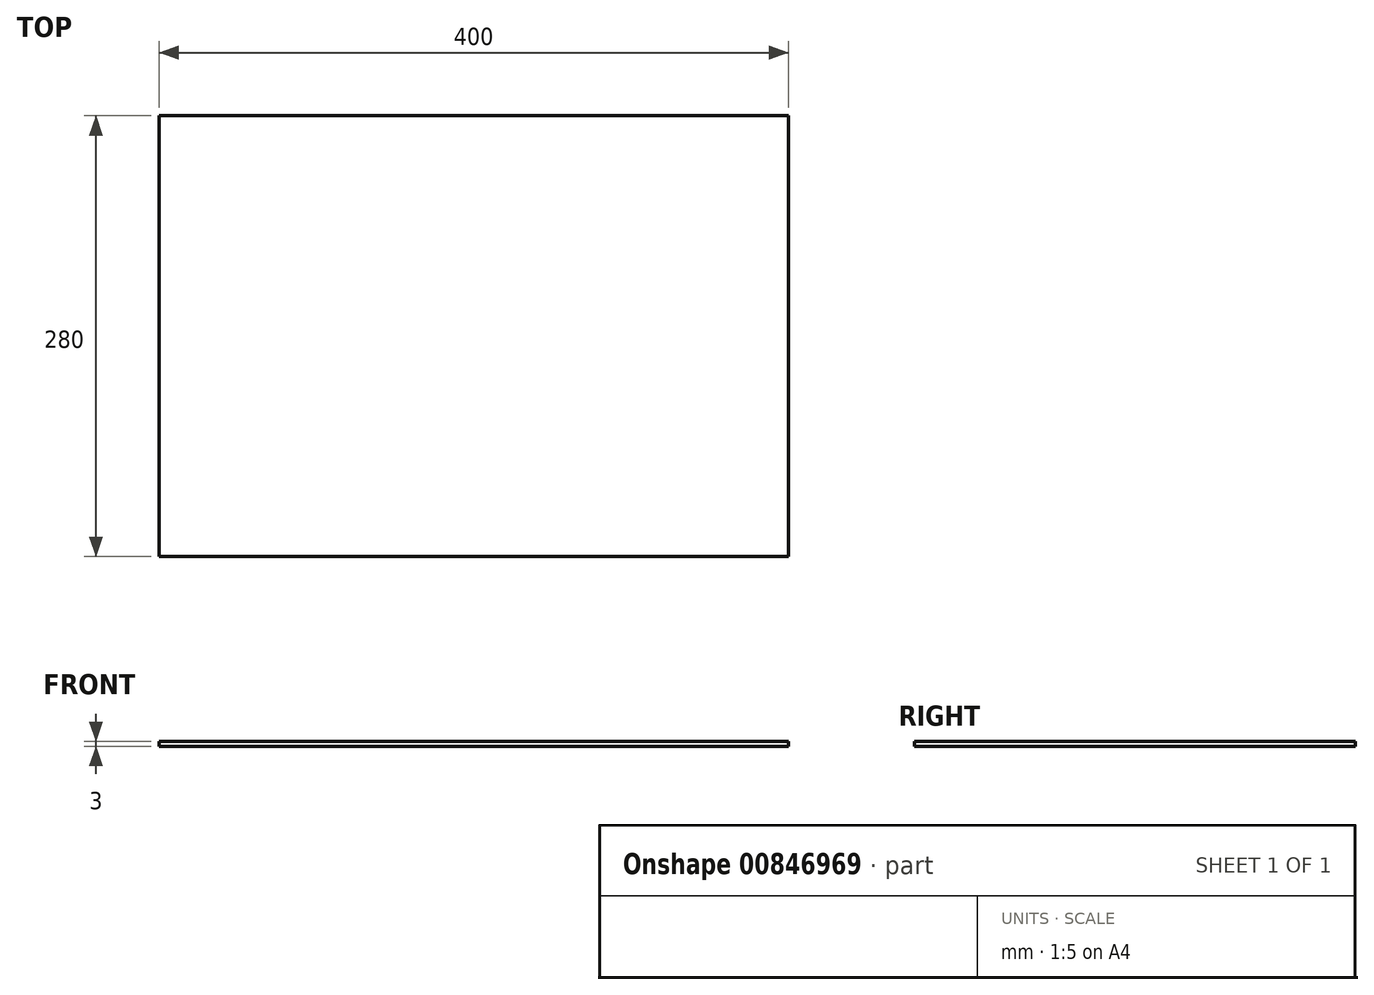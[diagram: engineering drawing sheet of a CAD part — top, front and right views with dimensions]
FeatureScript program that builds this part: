
annotation { "Feature Type Name" : "Feature", "Feature Type Description" : "" }
export const myFeature = defineFeature(function(context is Context, id is Id, definition is map)
    precondition{}
    {
        {
            var Q0;
            Q0=qCreatedBy(makeId("Top.planeOp"),FACE);
            var sketch = newSketch(context, id + "F0", { "sketchPlane" : qUnion([Q0])});
            skLineSegment(sketch, "E0.bottom", {"start": v(-200, 0) * mm, "end": v(200, 0) * mm});
            skLineSegment(sketch, "E0.top", {"start": v(-200, 280) * mm, "end": v(200, 280) * mm});
            skLineSegment(sketch, "E0.left", {"start": v(-200, 0) * mm, "end": v(-200, 280) * mm});
            skLineSegment(sketch, "E0.right", {"start": v(200, 0) * mm, "end": v(200, 280) * mm});
            skSolve(sketch);
        }
        {
            var Q0;
            Q0 = qSketchRegion(id + "F0", true);
            extrude(context, id + "F1", {"entities" : qUnion([Q0]), "depth" : 3 * mm, "offsetDistance" : 25 * mm});
        }
    });
